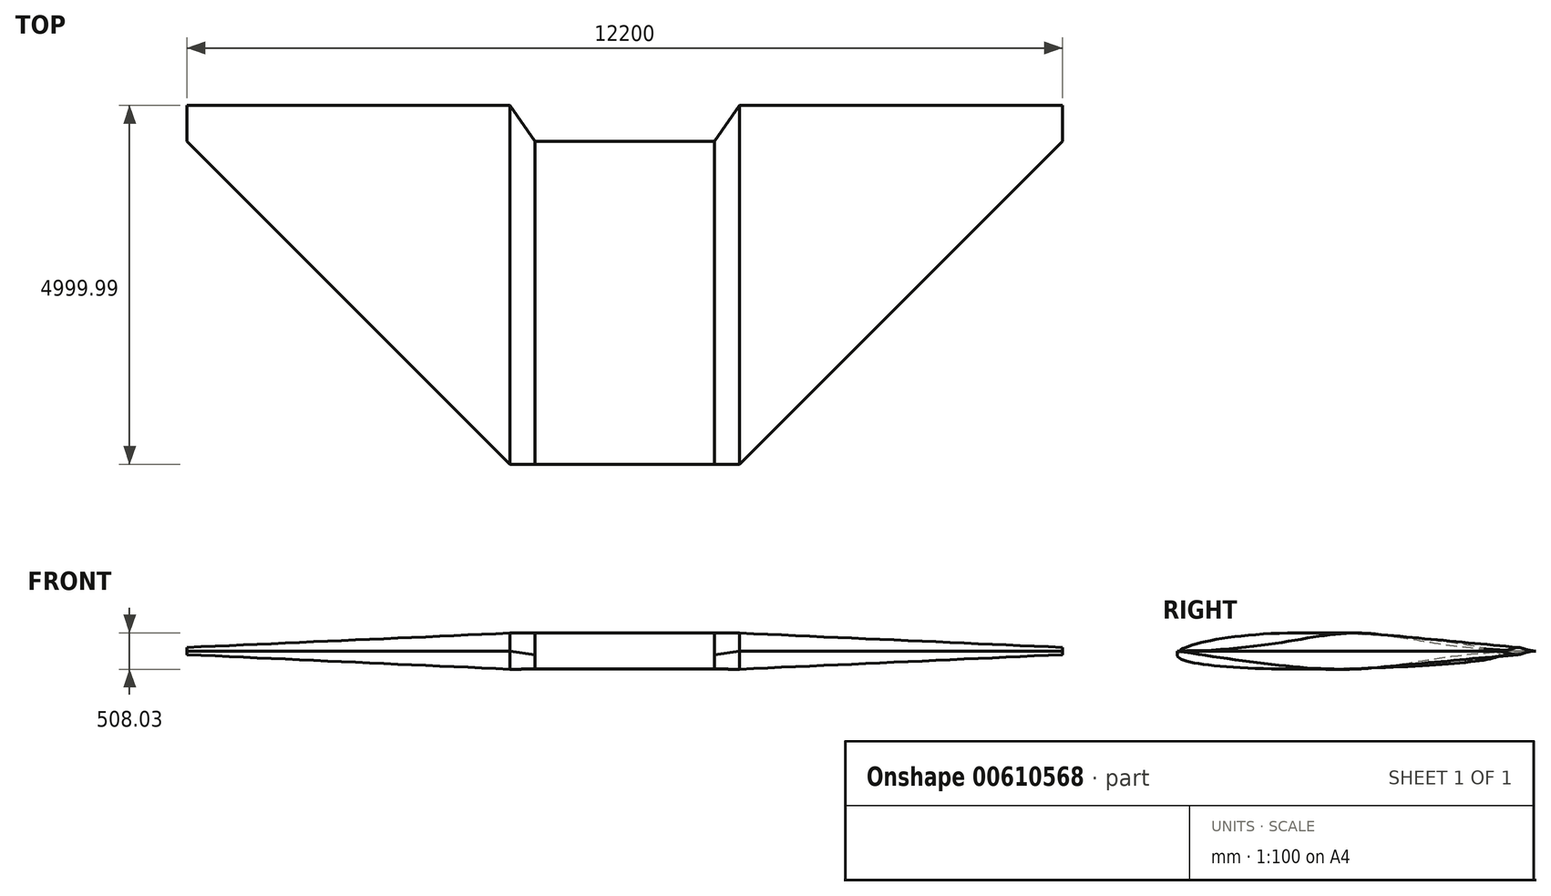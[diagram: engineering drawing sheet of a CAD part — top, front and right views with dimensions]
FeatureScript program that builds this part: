
annotation { "Feature Type Name" : "Feature", "Feature Type Description" : "" }
export const myFeature = defineFeature(function(context is Context, id is Id, definition is map)
    precondition{}
    {
        {
            var Q0;
            Q0=qCreatedBy(makeId("Right.planeOp"),FACE);
            var sketch = newSketch(context, id + "F0", { "sketchPlane" : qUnion([Q0])});
            skFitSpline(sketch, "E0", {"points": [v(-1500, -50) * mm, v(0, 250) * mm, v(3000, -50) * mm], "startDerivative": vector(0, 887.04) * mm, "endDerivative": vector(0, -631.84) * mm});
            skFitSpline(sketch, "E1", {"points": [v(-1500, -50) * mm, v(0, -250) * mm, v(3000, -50) * mm], "startDerivative": vector(0, -903.58) * mm, "endDerivative": vector(0, 641.04) * mm});
            skSolve(sketch);
        }
        {
            var Q0;
            Q0=qCreatedBy(makeId("Right.planeOp"),FACE);
            cPlane(context, id + "F1", {"entities" : qUnion([Q0]), "cplaneType" : CPlaneType.OFFSET, "offset" : 1600 * mm, "oppositeDirection" : true, "width" : 150 * mm, "height" : 150 * mm});
        }
        {
            var Q0;
            Q0=qCreatedBy(id+"F1.planeOp",FACE);
            var sketch = newSketch(context, id + "F2", { "sketchPlane" : qUnion([Q0])});
            skFitSpline(sketch, "E2", {"points": [v(-1500, 0) * mm, v(1000, 250) * mm, v(3500, 0) * mm], "startDerivative": vector(7500, 0) * mm, "endDerivative": vector(7500, 0) * mm});
            skFitSpline(sketch, "E3", {"points": [v(-1500, 0) * mm, v(1000, -250) * mm, v(3500, 0) * mm], "startDerivative": vector(5000, -750) * mm, "endDerivative": vector(7500, 0) * mm});
            skSolve(sketch);
        }
        {
            var Q0;
            Q0=qCreatedBy(makeId("Right.planeOp"),FACE);
            cPlane(context, id + "F3", {"entities" : qUnion([Q0]), "cplaneType" : CPlaneType.OFFSET, "offset" : 1600 * mm, "width" : 150 * mm, "height" : 150 * mm});
        }
        {
            var Q0;
            Q0=qCreatedBy(id+"F3.planeOp",FACE);
            var sketch = newSketch(context, id + "F4", { "sketchPlane" : qUnion([Q0])});
            skFitSpline(sketch, "E4", {"points": [v(-1500, 0) * mm, v(1000, 250) * mm, v(3500, 0) * mm], "startDerivative": vector(7500, 0) * mm, "endDerivative": vector(7500, 0) * mm});
            skFitSpline(sketch, "E5", {"points": [v(-1500, 0) * mm, v(1000, -250) * mm, v(3500, 0) * mm], "startDerivative": vector(5000, -750) * mm, "endDerivative": vector(7500, 0) * mm});
            skSolve(sketch);
        }
        {
            var Q0;
            Q0=qCreatedBy(makeId("Right.planeOp"),FACE);
            cPlane(context, id + "F5", {"entities" : qUnion([Q0]), "cplaneType" : CPlaneType.OFFSET, "offset" : 6100 * mm, "oppositeDirection" : true, "width" : 150 * mm, "height" : 150 * mm});
        }
        {
            var Q0;
            Q0=qCreatedBy(id+"F5.planeOp",FACE);
            var sketch = newSketch(context, id + "F6", { "sketchPlane" : qUnion([Q0])});
            skFitSpline(sketch, "E6", {"points": [v(3000, 0) * mm, v(3250, 50) * mm, v(3500, 0) * mm], "startDerivative": vector(750, 0) * mm, "endDerivative": vector(750, 0) * mm});
            skFitSpline(sketch, "E7", {"points": [v(3000, 0) * mm, v(3250, -50) * mm, v(3500, 0) * mm], "startDerivative": vector(500, -150) * mm, "endDerivative": vector(750, 0) * mm});
            skSolve(sketch);
        }
        {
            var Q0;
            Q0=qCreatedBy(makeId("Right.planeOp"),FACE);
            cPlane(context, id + "F7", {"entities" : qUnion([Q0]), "cplaneType" : CPlaneType.OFFSET, "offset" : 6100 * mm, "width" : 150 * mm, "height" : 150 * mm});
        }
        {
            var Q0;
            Q0=qCreatedBy(id+"F7.planeOp",FACE);
            var sketch = newSketch(context, id + "F8", { "sketchPlane" : qUnion([Q0])});
            skFitSpline(sketch, "E8", {"points": [v(3000, 0) * mm, v(3250, 50) * mm, v(3500, 0) * mm], "startDerivative": vector(750, 0) * mm, "endDerivative": vector(750, 0) * mm});
            skFitSpline(sketch, "E9", {"points": [v(3000, 0) * mm, v(3250, -50) * mm, v(3500, 0) * mm], "startDerivative": vector(500, -150) * mm, "endDerivative": vector(750, 0) * mm});
            skSolve(sketch);
        }
        {
            var Q0;
            Q0=makeQuery(id+"F0.imprint","IMPRINT",FACE,{"disambiguationData":[TD([[makeQuery(id+"F0.imprint","IMPRINT",EDGE,{"derivedFrom":sQuery(id+"F0.wireOp",EDGE,"E0")}),-1.0]])]});
            extrude(context, id + "F9", {"entities" : qUnion([Q0]), "endBound" : BoundingType.SYMMETRIC, "depth" : 2500 * mm, "offsetDistance" : 25 * mm});
        }
        {
            var Q1;
            Q1=makeQuery(id+"F9.opExtrude","CAP_FACE",FACE,{"disambiguationData":[OSD([sQuery(id+"F0.wireOp",EDGE,"E0"),sQuery(id+"F0.wireOp",EDGE,"E1")])],"isStart":true});
            var Q2;
            {var subQ0=sQuery(id+"F2.wireOp",EDGE,"E2");Q2=makeQuery(id+"F2.imprint","IMPRINT",FACE,{"disambiguationData":[TD([[makeQuery(id+"F2.imprint","IMPRINT",EDGE,{"derivedFrom":subQ0}),-1.0]])]});}
            loft(context, id + "F10", {"operationType" : NewBodyOperationType.ADD, "sheetProfilesArray" : [{ "sheetProfileEntities" : qUnion([Q1]) }, { "sheetProfileEntities" : qUnion([Q2]) }]});
        }
        {
            var Q1;
            Q1=makeQuery(id+"F9.opExtrude","CAP_FACE",FACE,{"disambiguationData":[OSD([sQuery(id+"F0.wireOp",EDGE,"E0"),sQuery(id+"F0.wireOp",EDGE,"E1")])],"isStart":false});
            var Q2;
            {var subQ0=sQuery(id+"F4.wireOp",EDGE,"E4");Q2=makeQuery(id+"F4.imprint","IMPRINT",FACE,{"disambiguationData":[TD([[makeQuery(id+"F4.imprint","IMPRINT",EDGE,{"derivedFrom":subQ0}),-1.0]])]});}
            loft(context, id + "F11", {"operationType" : NewBodyOperationType.ADD, "sheetProfilesArray" : [{ "sheetProfileEntities" : qUnion([Q1]) }, { "sheetProfileEntities" : qUnion([Q2]) }]});
        }
        {
            var Q1;
            {var subQ0=sQuery(id+"F2.wireOp",EDGE,"E2");Q1=makeQuery(id+"F10.opLoft","CAP_FACE",FACE,{"disambiguationData":[OSD([makeQuery(id+"F2.imprint","IMPRINT",FACE,{"disambiguationData":[TD([[makeQuery(id+"F2.imprint","IMPRINT",EDGE,{"derivedFrom":subQ0}),-1.0]])]})])],"isStart":true});}
            var Q2;
            {var subQ0=sQuery(id+"F6.wireOp",EDGE,"E6");Q2=makeQuery(id+"F6.imprint","IMPRINT",FACE,{"disambiguationData":[TD([[makeQuery(id+"F6.imprint","IMPRINT",EDGE,{"derivedFrom":subQ0}),-1.0]])]});}
            loft(context, id + "F12", {"operationType" : NewBodyOperationType.ADD, "sheetProfilesArray" : [{ "sheetProfileEntities" : qUnion([Q1]) }, { "sheetProfileEntities" : qUnion([Q2]) }]});
        }
        {
            var Q1;
            {var subQ0=sQuery(id+"F4.wireOp",EDGE,"E4");Q1=makeQuery(id+"F11.opLoft","CAP_FACE",FACE,{"disambiguationData":[OSD([makeQuery(id+"F4.imprint","IMPRINT",FACE,{"disambiguationData":[TD([[makeQuery(id+"F4.imprint","IMPRINT",EDGE,{"derivedFrom":subQ0}),-1.0]])]})])],"isStart":true});}
            var Q2;
            {var subQ0=sQuery(id+"F8.wireOp",EDGE,"E8");Q2=makeQuery(id+"F8.imprint","IMPRINT",FACE,{"disambiguationData":[TD([[makeQuery(id+"F8.imprint","IMPRINT",EDGE,{"derivedFrom":subQ0}),-1.0]])]});}
            loft(context, id + "F13", {"operationType" : NewBodyOperationType.ADD, "sheetProfilesArray" : [{ "sheetProfileEntities" : qUnion([Q1]) }, { "sheetProfileEntities" : qUnion([Q2]) }]});
        }
    });
